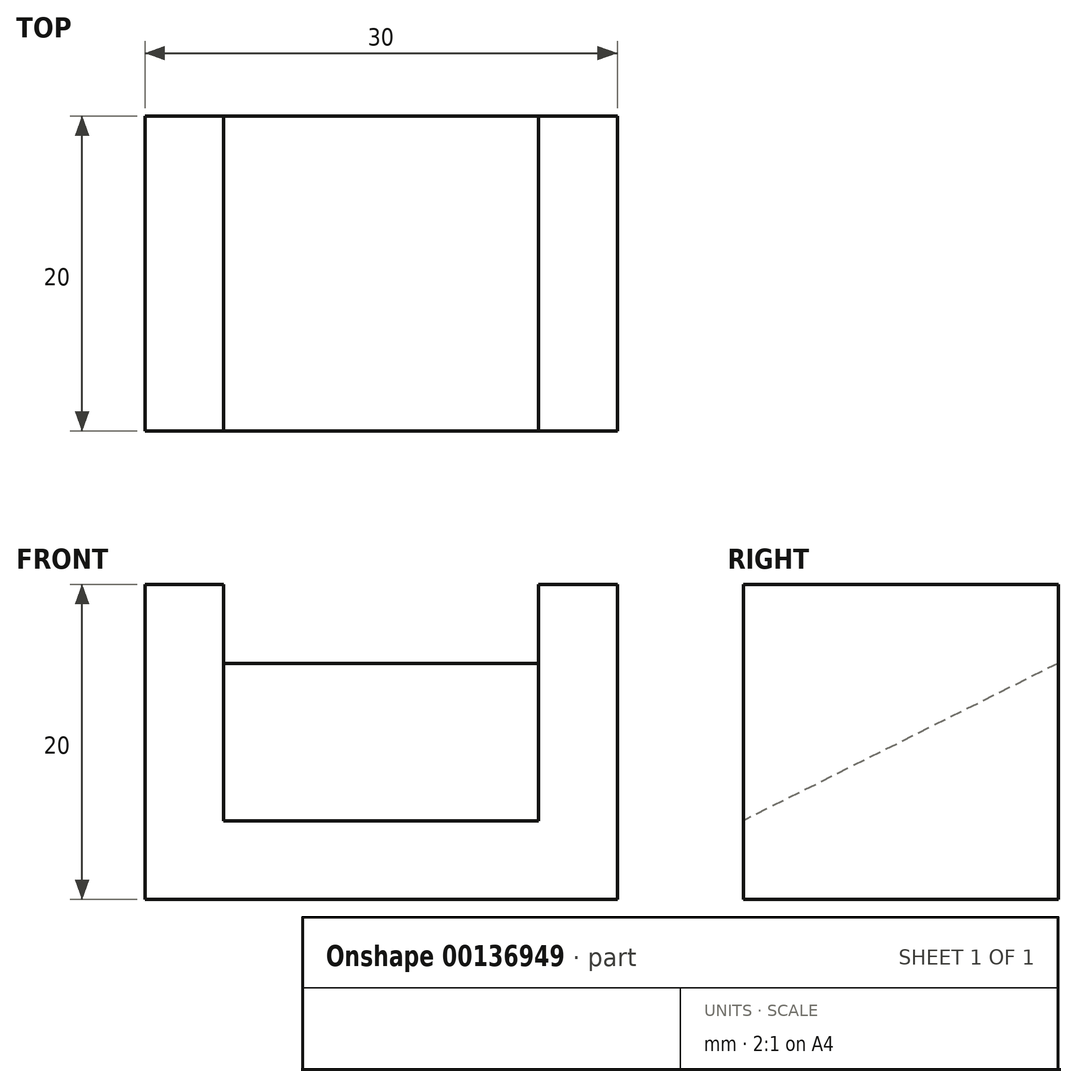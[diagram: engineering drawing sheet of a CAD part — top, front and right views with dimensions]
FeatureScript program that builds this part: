
annotation { "Feature Type Name" : "Feature", "Feature Type Description" : "" }
export const myFeature = defineFeature(function(context is Context, id is Id, definition is map)
    precondition{}
    {
        {
            var Q0;
            Q0=qCreatedBy(makeId("Right.planeOp"),FACE);
            var sketch = newSketch(context, id + "F0", { "sketchPlane" : qUnion([Q0])});
            skLineSegment(sketch, "E0.bottom", {"start": v(0, 0) * mm, "end": v(20, 0) * mm});
            skLineSegment(sketch, "E0.top", {"start": v(0, 20) * mm, "end": v(20, 20) * mm});
            skLineSegment(sketch, "E0.left", {"start": v(0, 0) * mm, "end": v(0, 20) * mm});
            skLineSegment(sketch, "E0.right", {"start": v(20, 0) * mm, "end": v(20, 20) * mm});
            skLineSegment(sketch, "E1", {"start": v(20, 15) * mm, "end": v(0, 5) * mm});
            skSolve(sketch);
        }
        {
            var Q0;
            Q0 = qSketchRegion(id + "F0", true);
            extrude(context, id + "F1", {"entities" : qUnion([Q0]), "depth" : 30 * mm});
        }
        {
            var Q0;
            Q0=makeQuery(id+"F1.opExtrude","CAP_FACE",FACE,{"disambiguationData":[OSD([sQuery(id+"F0.wireOp",EDGE,"E0.bottom"),sQuery(id+"F0.wireOp",EDGE,"E0.top"),sQuery(id+"F0.wireOp",EDGE,"E0.left"),sQuery(id+"F0.wireOp",EDGE,"E0.right")])],"isStart":false});
            var sketch = newSketch(context, id + "F2", { "sketchPlane" : qUnion([Q0])});
            skLineSegment(sketch, "E2.0", {"start": v(20, 15) * mm, "end": v(0, 5) * mm});
            skLineSegment(sketch, "E3.0", {"start": v(0, 0) * mm, "end": v(0, 20) * mm});
            skLineSegment(sketch, "E4.0", {"start": v(0, 20) * mm, "end": v(20, 20) * mm});
            skLineSegment(sketch, "E5.0", {"start": v(20, 0) * mm, "end": v(20, 20) * mm});
            skLineSegment(sketch, "E6.0", {"start": v(0, 0) * mm, "end": v(20, 0) * mm});
            skSolve(sketch);
        }
        {
            var Q0;
            {var subQ0=sQuery(id+"F2.wireOp",EDGE,"E2.0");Q0=makeQuery(id+"F2.imprint","IMPRINT",FACE,{"disambiguationData":[TD([[makeQuery(id+"F2.imprint","IMPRINT",EDGE,{"derivedFrom":subQ0}),-1.0]])]});}
            extrude(context, id + "F3", {"entities" : qUnion([Q0]), "operationType" : NewBodyOperationType.REMOVE, "oppositeDirection" : true, "depth" : 25 * mm, "hasSecondDirection" : true, "secondDirectionOppositeDirection" : true, "secondDirectionDepth" : 5 * mm});
        }
    });
